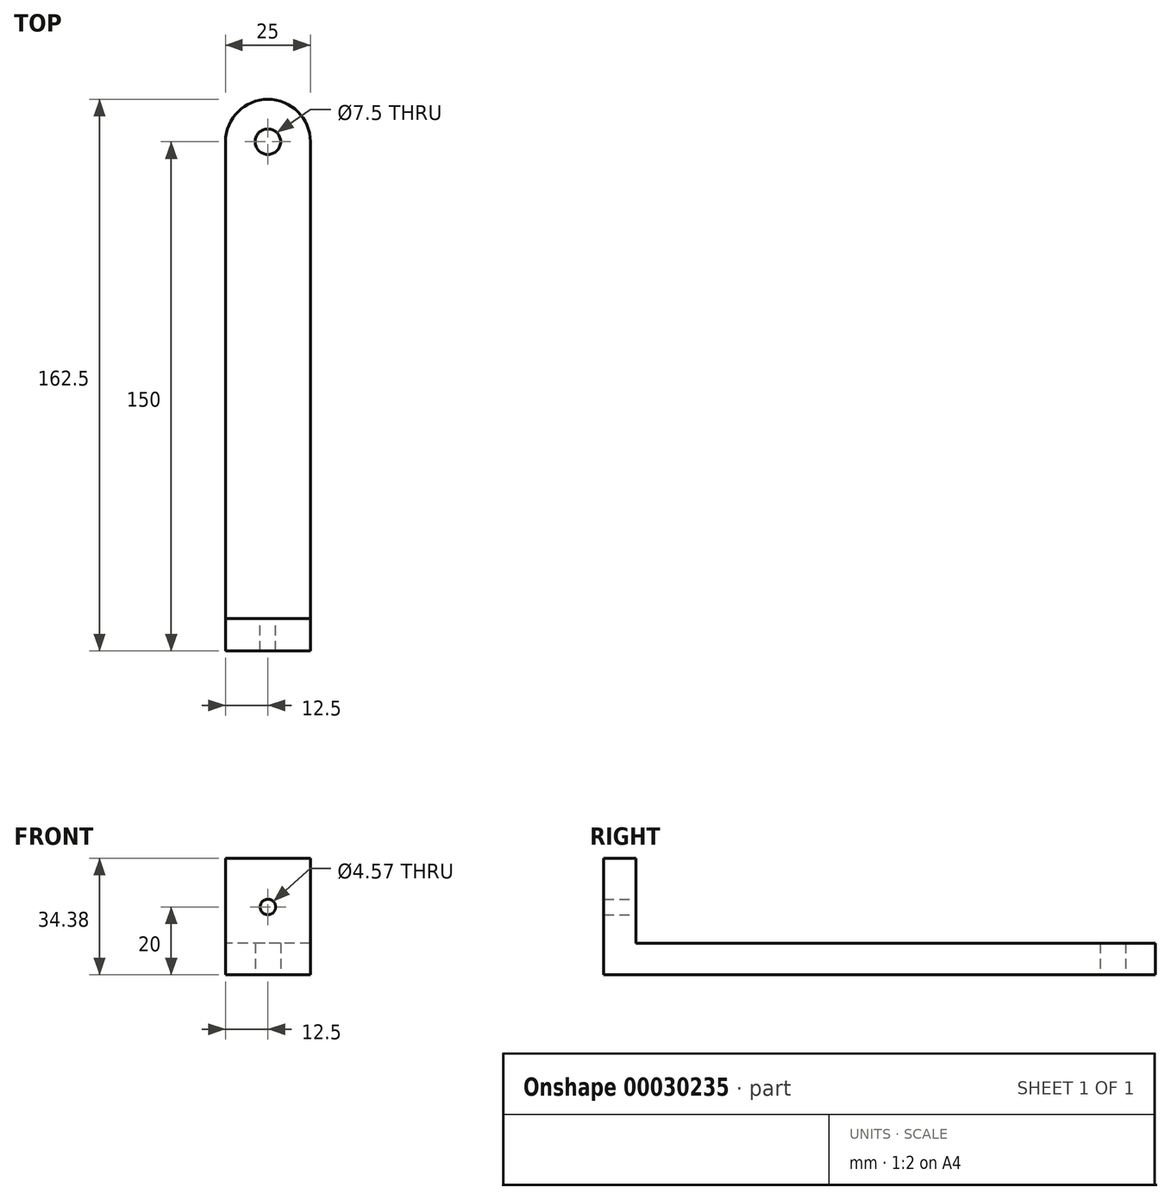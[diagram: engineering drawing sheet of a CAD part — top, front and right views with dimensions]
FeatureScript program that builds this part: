
annotation { "Feature Type Name" : "Feature", "Feature Type Description" : "" }
export const myFeature = defineFeature(function(context is Context, id is Id, definition is map)
    precondition{}
    {
        {
            var Q0;
            Q0=qCreatedBy(makeId("Top.planeOp"),FACE);
            var sketch = newSketch(context, id + "F0", { "sketchPlane" : qUnion([Q0])});
            skLineSegment(sketch, "E0.bottom", {"start": v(0, 0) * mm, "end": v(25, 0) * mm});
            skLineSegment(sketch, "E0.left", {"start": v(0, 0) * mm, "end": v(0, 150) * mm});
            skLineSegment(sketch, "E0.right", {"start": v(25, 0) * mm, "end": v(25, 150) * mm});
            skArc(sketch, "E1", {"start": v(0, 150) * mm, "mid": v(12.5, 162.5) * mm, "end": v(25, 150) * mm});
            skCircle(sketch, "E2", {"center": v(12.5, 150) * mm, "radius": 3.75 * mm});
            skSolve(sketch);
        }
        {
            var Q0;
            Q0=makeQuery(id+"F0.imprint","IMPRINT",FACE,{"disambiguationData":[TD([[makeQuery(id+"F0.imprint","IMPRINT",EDGE,{"derivedFrom":sQuery(id+"F0.wireOp",EDGE,"E0.bottom")}),1.0]])]});
            extrude(context, id + "F1", {"entities" : qUnion([Q0]), "depth" : 25 * 3 / 8 * mm});
        }
        {
            var Q0;
            Q0=makeQuery(id+"F1.opExtrude","CAP_FACE",FACE,{"disambiguationData":[OSD([sQuery(id+"F0.wireOp",EDGE,"E0.bottom"),sQuery(id+"F0.wireOp",EDGE,"E0.left"),sQuery(id+"F0.wireOp",EDGE,"E0.right"),sQuery(id+"F0.wireOp",EDGE,"E1"),sQuery(id+"F0.wireOp",EDGE,"E2")])],"isStart":false});
            var sketch = newSketch(context, id + "F2", { "sketchPlane" : qUnion([Q0])});
            skLineSegment(sketch, "E3.bottom", {"start": v(25, 0) * mm, "end": v(0, 0) * mm});
            skLineSegment(sketch, "E3.top", {"start": v(25, 9.52) * mm, "end": v(0, 9.52) * mm});
            skLineSegment(sketch, "E3.left", {"start": v(25, 0) * mm, "end": v(25, 9.52) * mm});
            skLineSegment(sketch, "E3.right", {"start": v(0, 0) * mm, "end": v(0, 9.52) * mm});
            skSolve(sketch);
        }
        {
            var Q0;
            Q0 = qSketchRegion(id + "F2", true);
            extrude(context, id + "F3", {"entities" : qUnion([Q0]), "operationType" : NewBodyOperationType.ADD, "depth" : 25 * mm});
        }
        {
            var Q0;
            Q0=makeQuery(id+"F3.opExtrude","SWEPT_FACE",FACE,{"disambiguationData":[OSD([sQuery(id+"F2.wireOp",EDGE,"E3.top")])]});
            var sketch = newSketch(context, id + "F4", { "sketchPlane" : qUnion([Q0])});
            skCircle(sketch, "E4", {"center": v(-12.5, 20) * mm, "radius": 2.28 * mm});
            skSolve(sketch);
        }
        {
            var Q0;
            Q0 = qSketchRegion(id + "F4", true);
            extrude(context, id + "F5", {"entities" : qUnion([Q0]), "operationType" : NewBodyOperationType.REMOVE, "endBound" : BoundingType.UP_TO_NEXT, "oppositeDirection" : true, "depth" : 25 * mm});
        }
    });
